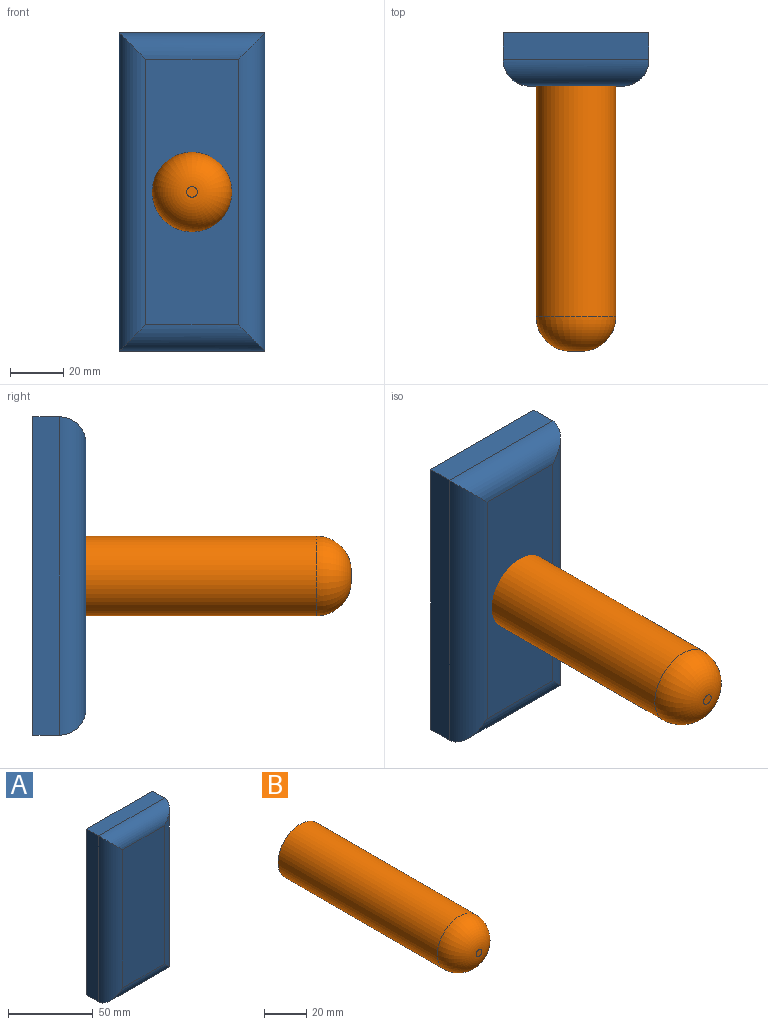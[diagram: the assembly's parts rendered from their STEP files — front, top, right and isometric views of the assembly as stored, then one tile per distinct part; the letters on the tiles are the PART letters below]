
ASSEMBLY  parts=2 mates=1
PART A: 10 faces, bbox 55x20x120 mm
  f0: plane 55x10mm, normal (0,0,1), area 550mm2, adj f1,f3,f5,f6
  f1: plane 120x10mm, normal (-1,0,0), area 1200mm2, adj f0,f2,f5,f7
  f2: plane 55x10mm, normal (0,0,-1), area 550mm2, adj f1,f3,f5,f9
  f3: plane 120x10mm, normal (1,0,0), area 1200mm2, adj f0,f2,f5,f8
  f4: plane 100x35mm, normal (0,-1,0), area 3500mm2, adj f6,f7,f8,f9
  f5: plane 120x55mm, normal (0,1,0), area 6600mm2, adj f0,f1,f2,f3
  f6: cylinder r=10mm len=55mm, axis (1,0,0), area 749.8mm2, adj f0,f4,f7,f8
  f7: cylinder r=10mm len=120mm, axis (0,0,1), area 1770.8mm2, adj f1,f4,f6,f9
  f8: cylinder r=10mm len=120mm, axis (0,0,-1), area 1770.8mm2, adj f3,f4,f6,f9
  f9: cylinder r=10mm len=55mm, axis (-1,0,0), area 749.8mm2, adj f2,f4,f7,f8
PART B: 4 faces, bbox 30x120x30 mm
  f0: cylinder r=15mm len=107mm, axis (0,1,0), area 10084.5mm2, adj f2,f3
  f1: plane 4x4mm, normal (0,-1,0), area 12.6mm2, adj f3
  f2: plane 30x30mm, normal (0,1,0), area 706.9mm2, adj f0
  f3: torus R=2mm, axis (0,-1,0), area 1318.5mm2, adj f0,f1
PLACE A t=(17.91,20.99,-3.49)mm
PLACE B t=(9.75,20.99,8.05)mm
MATE fastened B.f0 <-> A.f5  axis (0,1,0) through (9.75,20.99,8.05)mm
